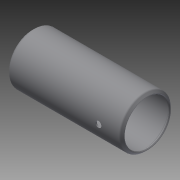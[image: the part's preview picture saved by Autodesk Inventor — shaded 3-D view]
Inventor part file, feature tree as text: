
AUTODESK INVENTOR PART (.ipt)
format: ipt  version: 2014 SP2 (Build 180246200, 246)  size: 161,792 bytes
history: native  units: in
note: dims shown in document units (in); Inventor stores cm internally (conversion verified against a paired STEP export)
features: other x42, sketch x2, revolve x1, extrude x1
ambient origin geometry x8: Origin, YZ Plane, XZ Plane, XY Plane, X Axis, Y Axis, Z Axis, Center Point
bodies: Solid1 (feature_tree)
feature tree (46):
  revolve  "Revolution1"  [1 undecoded]
  extrude  "Extrusion1"  [1 undecoded]
  other  "cp1_XY"
  other  "cp1_YZ"
  other  "cp1_ZX"
  other  "cp1_X"
  other  "cp1_Y"
  other  "cp1_Z"
  other  "cp1_Center"
  other  "cp2_XY"
  other  "cp2_YZ"
  other  "cp2_ZX"
  other  "cp2_X"
  other  "cp2_Y"
  other  "cp2_Z"
  other  "cp2_Center"
  other  "cp3_XY"
  other  "cp3_YZ"
  other  "cp3_ZX"
  other  "cp3_X"
  other  "cp3_Y"
  other  "cp3_Z"
  other  "cp3_Center"
  other  "cp4_XY"
  other  "cp4_YZ"
  other  "cp4_ZX"
  other  "cp4_X"
  other  "cp4_Y"
  other  "cp4_Z"
  other  "cp4_Center"
  other  "tube_front_XY"
  other  "tube_front_YZ"
  other  "tube_front_ZX"
  other  "tube_front_X"
  other  "tube_front_Y"
  other  "tube_front_Z"
  other  "tube_front_Center"
  other  "tube_rear_XY"
  other  "tube_rear_YZ"
  other  "tube_rear_ZX"
  other  "tube_rear_X"
  other  "tube_rear_Y"
  other  "tube_rear_Z"
  other  "tube_rear_Center"
  sketch  "Sketch_1"  dims[d0=360.0deg d1=0.4038in d2=0.0in]
  sketch  "Sketch_7"
note: 2 required parameter values undecoded (feature->parameter linkage not recoverable at this tier; creation-order binding heuristic only, values carry confidence <= 0.55)